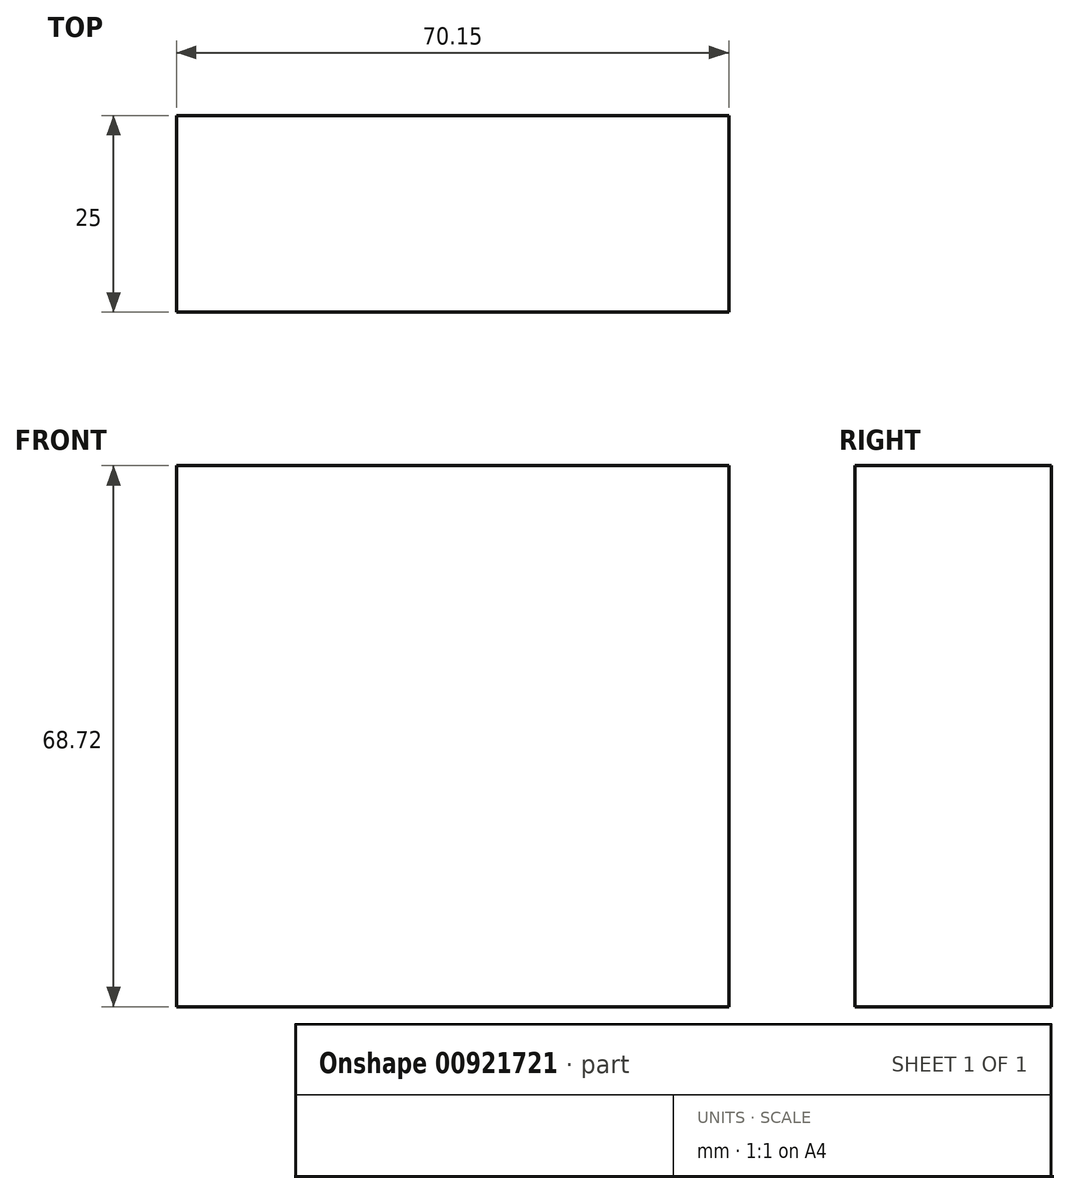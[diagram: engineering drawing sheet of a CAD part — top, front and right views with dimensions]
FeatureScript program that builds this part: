
annotation { "Feature Type Name" : "Feature", "Feature Type Description" : "" }
export const myFeature = defineFeature(function(context is Context, id is Id, definition is map)
    precondition{}
    {
        {
            var Q0;
            Q0=qCreatedBy(makeId("Front.planeOp"),FACE);
            var sketch = newSketch(context, id + "F0", { "sketchPlane" : qUnion([Q0])});
            skLineSegment(sketch, "E0.bottom", {"start": v(-121.47, 54.33) * mm, "end": v(-51.32, 54.33) * mm});
            skLineSegment(sketch, "E0.top", {"start": v(-121.47, -14.39) * mm, "end": v(-51.32, -14.39) * mm});
            skLineSegment(sketch, "E0.left", {"start": v(-121.47, 54.33) * mm, "end": v(-121.47, -14.39) * mm});
            skLineSegment(sketch, "E0.right", {"start": v(-51.32, 54.33) * mm, "end": v(-51.32, -14.39) * mm});
            skSolve(sketch);
        }
        {
            var Q0;
            Q0 = qSketchRegion(id + "F0", true);
            extrude(context, id + "F1", {"entities" : qUnion([Q0]), "depth" : 25 * mm, "offsetDistance" : 25 * mm});
        }
    });
